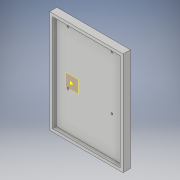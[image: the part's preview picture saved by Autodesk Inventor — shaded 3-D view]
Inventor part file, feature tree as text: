
AUTODESK INVENTOR PART (.ipt)
format: ipt  version: 2019.4 (Build 234330000, 330)  size: 156,160 bytes
history: native  units: in
note: dims shown in document units (in); Inventor stores cm internally (conversion verified against a paired STEP export)
features: sketch x7, extrude x6, plane x1
ambient origin geometry x8: Origin, YZ Plane, XZ Plane, XY Plane, X Axis, Y Axis, Z Axis, Center Point
bodies: Solid1 (feature_tree)
feature tree (14):
  sketch  "Sketch1"  dims[d0=5.0in d1=7.0in]
  plane  "Work Plane1"
  sketch  "Sketch3"  dims[d4=0.135in d7=2.0in]
  extrude  "Extrusion3"  Depth=7.0in
  extrude  "Extrusion4"  Depth=2.0in
  sketch  "Sketch4"  dims[d14=0.135in d15=0.135in]
  extrude  "Extrusion5"  Depth=0.135in
  extrude  "Extrusion6"  Depth=3.0in
  extrude  "Extrusion7"  Depth=3.65in
  extrude  "Extrusion8"  Depth=1.0in
  sketch  "Sketch6"  dims[d16=0.135in d17=3.0in]
  sketch  "Sketch7"  dims[d18=3.65in d19=3.65in]
  sketch  "Sketch8"  dims[d20=3.0in d21=1.0in]
  sketch  "Sketch9"  dims[d22=0.5in d23=0.5in d26=0.25in d27=0.0in d28=0.25in d29=0.0in d34=0.2in d35=0.2in d36=0.2in d37=0.2in d38=0.25in d39=0.0in d40=0.2in d41=0.25in d42=0.0in d43=0.2in d44=6.8in d45=0.25in d46=0.0in d47=4.6in d48=0.2in d49=0.25in d50=0.0in]
